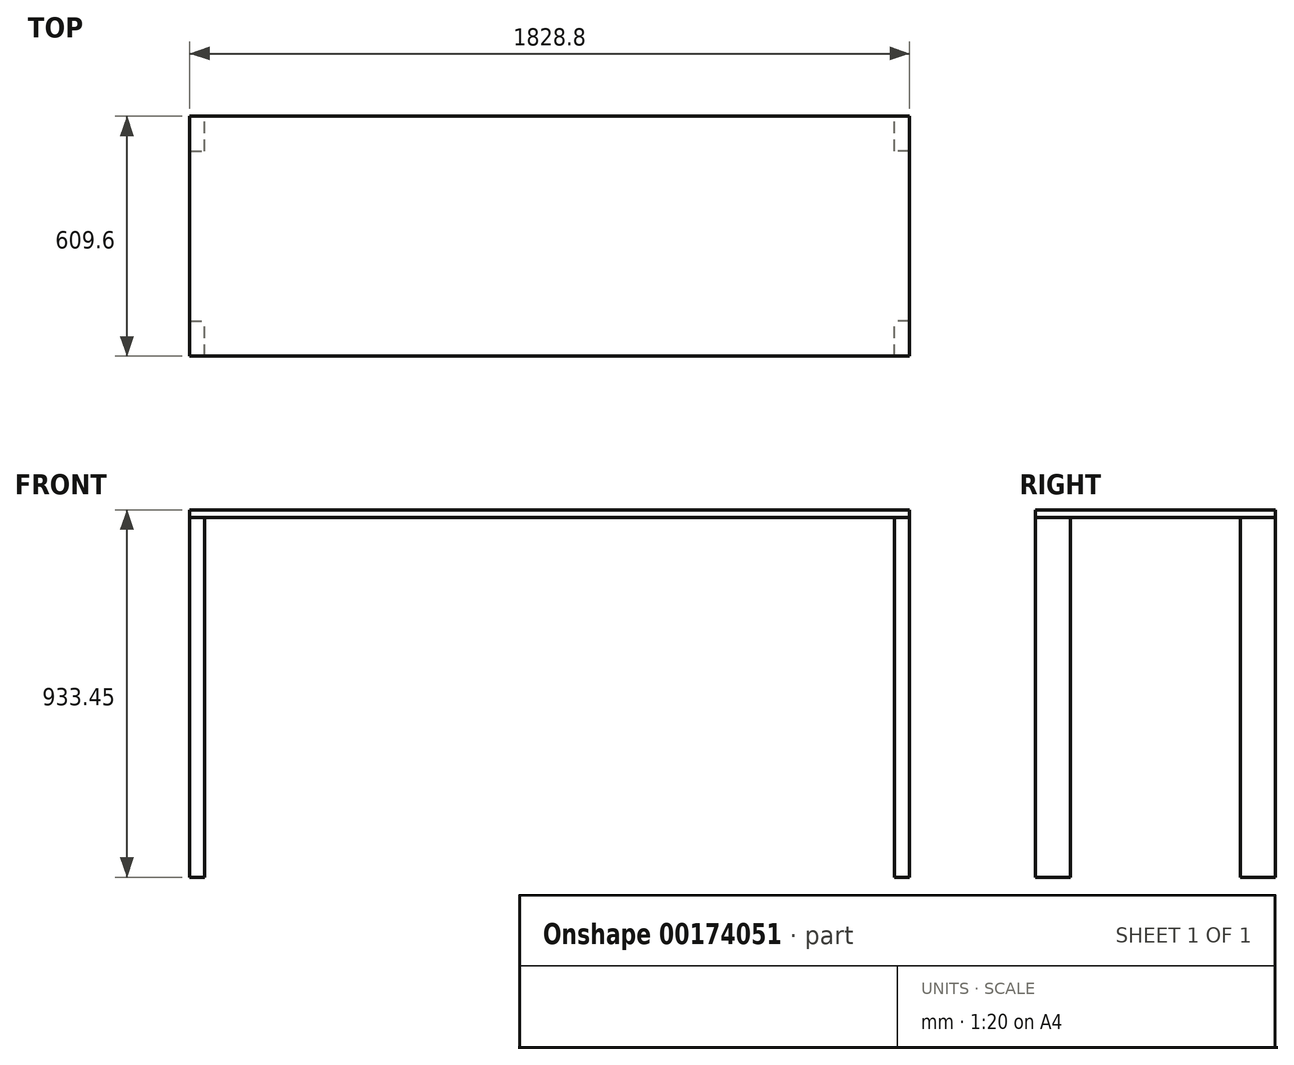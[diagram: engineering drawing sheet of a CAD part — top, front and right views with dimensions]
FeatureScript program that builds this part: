
annotation { "Feature Type Name" : "Feature", "Feature Type Description" : "" }
export const myFeature = defineFeature(function(context is Context, id is Id, definition is map)
    precondition{}
    {
        {
            var Q0;
            Q0=qCreatedBy(makeId("Top.planeOp"),FACE);
            var sketch = newSketch(context, id + "F0", { "sketchPlane" : qUnion([Q0])});
            skLineSegment(sketch, "E0.bottom", {"start": v(-914.4, 0) * mm, "end": v(-876.3, 0) * mm});
            skLineSegment(sketch, "E0.top", {"start": v(-914.4, 88.9) * mm, "end": v(-876.3, 88.9) * mm});
            skLineSegment(sketch, "E0.left", {"start": v(-914.4, 0) * mm, "end": v(-914.4, 88.9) * mm});
            skLineSegment(sketch, "E0.right", {"start": v(-876.3, 0) * mm, "end": v(-876.3, 88.9) * mm});
            skLineSegment(sketch, "E1.bottom", {"start": v(-914.4, 520.7) * mm, "end": v(-876.3, 520.7) * mm});
            skLineSegment(sketch, "E1.top", {"start": v(-914.4, 609.6) * mm, "end": v(-876.3, 609.6) * mm});
            skLineSegment(sketch, "E1.left", {"start": v(-914.4, 520.7) * mm, "end": v(-914.4, 609.6) * mm});
            skLineSegment(sketch, "E1.right", {"start": v(-876.3, 520.7) * mm, "end": v(-876.3, 609.6) * mm});
            skSolve(sketch);
        }
        {
            var Q0;
            Q0=makeQuery(id+"F0.imprint","IMPRINT",FACE,{"disambiguationData":[TD([[makeQuery(id+"F0.imprint","IMPRINT",EDGE,{"derivedFrom":sQuery(id+"F0.wireOp",EDGE,"E1.bottom")}),1.0]])]});
            var Q1;
            Q1=makeQuery(id+"F0.imprint","IMPRINT",FACE,{"disambiguationData":[TD([[makeQuery(id+"F0.imprint","IMPRINT",EDGE,{"derivedFrom":sQuery(id+"F0.wireOp",EDGE,"E0.bottom")}),1.0]])]});
            extrude(context, id + "F1", {"entities" : qUnion([Q0, Q1]), "depth" : 914.4 * mm});
        }
        {
            var Q0;
            Q0=makeQuery(id+"F1.opExtrude","SWEPT_BODY",BODY,{"disambiguationData":[OSD([sQuery(id+"F0.wireOp",EDGE,"E0.bottom"),sQuery(id+"F0.wireOp",EDGE,"E0.top"),sQuery(id+"F0.wireOp",EDGE,"E0.left"),sQuery(id+"F0.wireOp",EDGE,"E0.right")])]});
            var Q1;
            Q1=makeQuery(id+"F1.opExtrude","SWEPT_BODY",BODY,{"disambiguationData":[OSD([sQuery(id+"F0.wireOp",EDGE,"E1.bottom"),sQuery(id+"F0.wireOp",EDGE,"E1.top"),sQuery(id+"F0.wireOp",EDGE,"E1.left"),sQuery(id+"F0.wireOp",EDGE,"E1.right")])]});
            var Q2;
            Q2=qCreatedBy(makeId("Right.planeOp"),FACE);
            mirror(context, id + "F2", {"entities" : qUnion([Q0, Q1]), "mirrorPlane" : qUnion([Q2])});
        }
        {
            var Q0;
            Q0=qCreatedBy(makeId("Top.planeOp"),FACE);
            var Q1;
            Q1=makeQuery(id+"F1.opExtrude","CAP_VERTEX",VERTEX,{"disambiguationData":[OSD([sQuery(id+"F0.wireOp",EDGE,"E0.bottom"),sQuery(id+"F0.wireOp",EDGE,"E0.left")])],"isStart":false});
            cPlane(context, id + "F3", {"entities" : qUnion([Q0, Q1]), "cplaneType" : CPlaneType.PLANE_POINT, "offset" : 25.4 * mm, "width" : 152.4 * mm, "height" : 152.4 * mm});
        }
        {
            var Q0;
            Q0=qCreatedBy(id+"F3.planeOp",FACE);
            var sketch = newSketch(context, id + "F4", { "sketchPlane" : qUnion([Q0])});
            skLineSegment(sketch, "E2.0.0", {"start": v(-914.4, 609.6) * mm, "end": v(-914.4, 520.7) * mm, "construction": true});
            skLineSegment(sketch, "E2.0.1", {"start": v(-914.4, 520.7) * mm, "end": v(-876.3, 520.7) * mm, "construction": true});
            skLineSegment(sketch, "E2.0.2", {"start": v(-876.3, 520.7) * mm, "end": v(-876.3, 609.6) * mm, "construction": true});
            skLineSegment(sketch, "E2.0.3", {"start": v(-876.3, 609.6) * mm, "end": v(-914.4, 609.6) * mm, "construction": true});
            skLineSegment(sketch, "E3.0.0", {"start": v(-914.4, 88.9) * mm, "end": v(-914.4, 0) * mm, "construction": true});
            skLineSegment(sketch, "E3.0.1", {"start": v(-914.4, 0) * mm, "end": v(-876.3, 0) * mm, "construction": true});
            skLineSegment(sketch, "E3.0.2", {"start": v(-876.3, 0) * mm, "end": v(-876.3, 88.9) * mm, "construction": true});
            skLineSegment(sketch, "E3.0.3", {"start": v(-876.3, 88.9) * mm, "end": v(-914.4, 88.9) * mm, "construction": true});
            skLineSegment(sketch, "E4.0.0", {"start": v(914.4, 520.7) * mm, "end": v(914.4, 609.6) * mm, "construction": true});
            skLineSegment(sketch, "E4.0.1", {"start": v(914.4, 609.6) * mm, "end": v(876.3, 609.6) * mm, "construction": true});
            skLineSegment(sketch, "E4.0.2", {"start": v(876.3, 609.6) * mm, "end": v(876.3, 520.7) * mm, "construction": true});
            skLineSegment(sketch, "E4.0.3", {"start": v(876.3, 520.7) * mm, "end": v(914.4, 520.7) * mm, "construction": true});
            skLineSegment(sketch, "E5.0.0", {"start": v(914.4, 0) * mm, "end": v(914.4, 88.9) * mm, "construction": true});
            skLineSegment(sketch, "E5.0.1", {"start": v(914.4, 88.9) * mm, "end": v(876.3, 88.9) * mm, "construction": true});
            skLineSegment(sketch, "E5.0.2", {"start": v(876.3, 88.9) * mm, "end": v(876.3, 0) * mm, "construction": true});
            skLineSegment(sketch, "E5.0.3", {"start": v(876.3, 0) * mm, "end": v(914.4, 0) * mm, "construction": true});
            skLineSegment(sketch, "E6.bottom", {"start": v(-914.4, 609.6) * mm, "end": v(914.4, 609.6) * mm});
            skLineSegment(sketch, "E6.top", {"start": v(-914.4, 0) * mm, "end": v(914.4, 0) * mm});
            skLineSegment(sketch, "E6.left", {"start": v(-914.4, 609.6) * mm, "end": v(-914.4, 0) * mm});
            skLineSegment(sketch, "E6.right", {"start": v(914.4, 609.6) * mm, "end": v(914.4, 0) * mm});
            skSolve(sketch);
        }
        {
            var Q0;
            Q0=makeQuery(id+"F4.imprint","IMPRINT",FACE,{"disambiguationData":[TD([[makeQuery(id+"F4.imprint","IMPRINT",EDGE,{"derivedFrom":sQuery(id+"F4.wireOp",EDGE,"E6.bottom")}),-1.0]])]});
            extrude(context, id + "F5", {"entities" : qUnion([Q0]), "depth" : 19.05 * mm});
        }
    });
